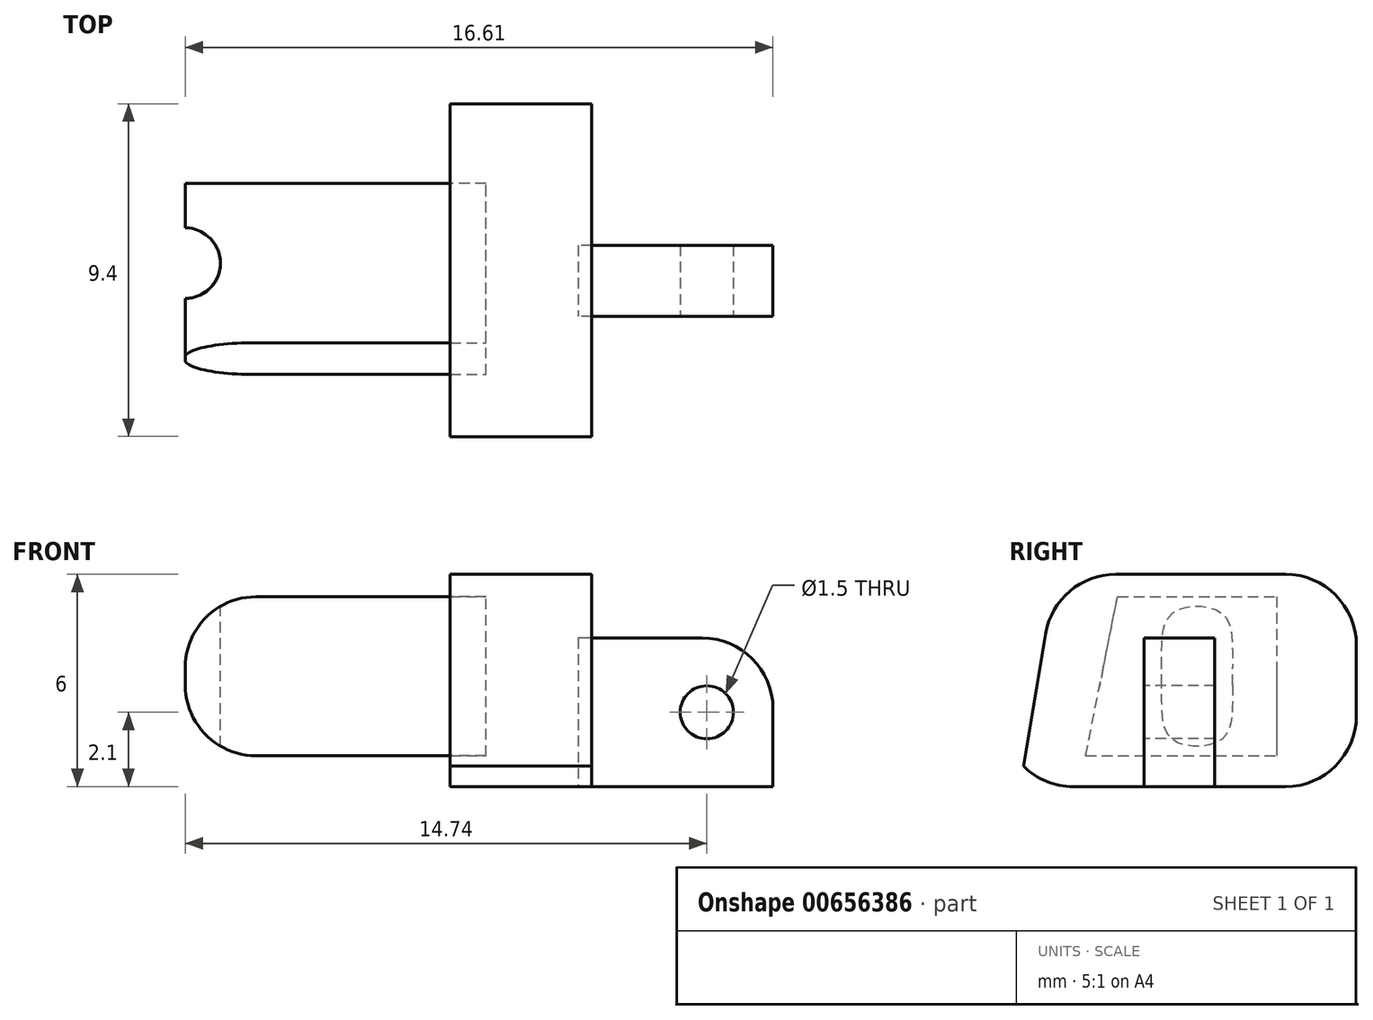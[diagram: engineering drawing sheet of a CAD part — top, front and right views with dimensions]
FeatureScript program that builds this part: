
annotation { "Feature Type Name" : "Feature", "Feature Type Description" : "" }
export const myFeature = defineFeature(function(context is Context, id is Id, definition is map)
    precondition{}
    {
        {
            var Q0;
            Q0=qCreatedBy(makeId("Top.planeOp"),FACE);
            var sketch = newSketch(context, id + "F0", { "sketchPlane" : qUnion([Q0])});
            skLineSegment(sketch, "E0.bottom", {"start": v(2, -5) * mm, "end": v(-2, -5) * mm});
            skLineSegment(sketch, "E0.top", {"start": v(2, 5) * mm, "end": v(-2, 5) * mm});
            skLineSegment(sketch, "E0.left", {"start": v(2, -5) * mm, "end": v(2, 5) * mm});
            skLineSegment(sketch, "E0.right", {"start": v(-2, -5) * mm, "end": v(-2, 5) * mm});
            skPoint(sketch, "E0.middle", {"position": v(0, 0) * mm});
            skLineSegment(sketch, "E1.bottom", {"start": v(8.83, 1) * mm, "end": v(3.33, 1) * mm});
            skLineSegment(sketch, "E1.top", {"start": v(8.83, -1) * mm, "end": v(3.33, -1) * mm});
            skLineSegment(sketch, "E1.left", {"start": v(8.83, 1) * mm, "end": v(8.83, -1) * mm});
            skLineSegment(sketch, "E1.right", {"start": v(3.33, 1) * mm, "end": v(3.33, -1) * mm});
            skPoint(sketch, "E1.middle", {"position": v(6.08, 0) * mm});
            skPoint(sketch, "E2.middle", {"position": v(-8.35, 0) * mm});
            skLineSegment(sketch, "E3.bottom", {"start": v(-3.78, -2.75) * mm, "end": v(-12.28, -2.75) * mm});
            skLineSegment(sketch, "E3.top", {"start": v(-3.78, 2.75) * mm, "end": v(-12.28, 2.75) * mm});
            skLineSegment(sketch, "E3.left", {"start": v(-3.78, -2.75) * mm, "end": v(-3.78, 2.75) * mm});
            skLineSegment(sketch, "E3.right", {"start": v(-12.28, -2.75) * mm, "end": v(-12.28, 2.75) * mm});
            skPoint(sketch, "E3.middle", {"position": v(-8.03, 0) * mm});
            skLineSegment(sketch, "E4", {"start": v(0, 0) * mm, "end": v(-1.4, 0) * mm, "construction": true});
            skLineSegment(sketch, "E5", {"start": v(-20.62, 0) * mm, "end": v(21.03, 0) * mm, "construction": true});
            skSolve(sketch);
        }
        {
            var Q0;
            Q0=makeQuery(id+"F0.imprint","IMPRINT",FACE,{"disambiguationData":[TD([[makeQuery(id+"F0.imprint","IMPRINT",EDGE,{"derivedFrom":sQuery(id+"F0.wireOp",EDGE,"E0.bottom")}),-1.0]])]});
            extrude(context, id + "F1", {"entities" : qUnion([Q0]), "depth" : 6 * mm, "offsetDistance" : 25 * mm});
        }
        {
            var Q0;
            Q0=makeQuery(id+"F0.imprint","IMPRINT",FACE,{"disambiguationData":[TD([[makeQuery(id+"F0.imprint","IMPRINT",EDGE,{"derivedFrom":sQuery(id+"F0.wireOp",EDGE,"E1.bottom")}),1.0]])]});
            extrude(context, id + "F2", {"entities" : qUnion([Q0]), "depth" : 4.2 * mm, "offsetDistance" : 25 * mm});
        }
        {
            var Q0;
            Q0=makeQuery(id+"F0.imprint","IMPRINT",FACE,{"disambiguationData":[TD([[makeQuery(id+"F0.imprint","IMPRINT",EDGE,{"derivedFrom":sQuery(id+"F0.wireOp",EDGE,"E3.bottom")}),-1.0]])]});
            extrude(context, id + "F3", {"entities" : qUnion([Q0]), "depth" : 4.5 * mm, "offsetDistance" : 25 * mm});
        }
        {
            var Q0;
            Q0=makeQuery(id+"F2.opExtrude","SWEPT_BODY",BODY,{"disambiguationData":[OSD([sQuery(id+"F0.wireOp",EDGE,"E1.bottom"),sQuery(id+"F0.wireOp",EDGE,"E1.top"),sQuery(id+"F0.wireOp",EDGE,"E1.left"),sQuery(id+"F0.wireOp",EDGE,"E1.right")])]});
            transform(context, id + "F4", {"entities" : qUnion([Q0]), "transformType" : TransformType.TRANSLATION_3D, "dx" : -1.71 * mm, "dy" : 0 * mm, "dz" : 0 * mm, "makeCopy" : false});
        }
        {
            var Q0;
            Q0=makeQuery(id+"F3.opExtrude","SWEPT_BODY",BODY,{"disambiguationData":[OSD([sQuery(id+"F0.wireOp",EDGE,"E3.bottom"),sQuery(id+"F0.wireOp",EDGE,"E3.top"),sQuery(id+"F0.wireOp",EDGE,"E3.left"),sQuery(id+"F0.wireOp",EDGE,"E3.right")])]});
            transform(context, id + "F5", {"entities" : qUnion([Q0]), "transformType" : TransformType.TRANSLATION_3D, "dx" : 2.8 * mm, "dy" : 0 * mm, "dz" : 0.87 * mm, "makeCopy" : false});
        }
        {
            var Q0;
            Q0=makeQuery(id+"F1.opExtrude","CAP_EDGE",EDGE,{"disambiguationData":[OSD([sQuery(id+"F0.wireOp",EDGE,"E0.bottom")])],"isStart":true});
            fillet(context, id + "F6", {"entities" : qUnion([Q0]), "radius" : 2 * mm, "tangentPropagation" : true, "allowEdgeOverflow" : false});
        }
        {
            var Q0;
            Q0=makeQuery(id+"F1.opExtrude","CAP_EDGE",EDGE,{"disambiguationData":[OSD([sQuery(id+"F0.wireOp",EDGE,"E0.bottom")])],"isStart":false});
            chamfer(context, id + "F7", {"entities" : qUnion([Q0]), "chamferType" : ChamferType.TWO_OFFSETS, "width1" : 9 * mm, "oppositeDirection" : false, "width2" : 1.5 * mm, "tangentPropagation" : true});
        }
        {
            var Q0;
            Q0=makeQuery(id+"F2.opExtrude","SWEPT_FACE",FACE,{"disambiguationData":[OSD([sQuery(id+"F0.wireOp",EDGE,"E1.top")])]});
            var sketch = newSketch(context, id + "F8", { "sketchPlane" : qUnion([Q0])});
            skCircle(sketch, "E6", {"center": v(5.25, 2.1) * mm, "radius": 0.75 * mm});
            skSolve(sketch);
        }
        {
            var Q0;
            Q0=makeQuery(id+"F8.imprint","IMPRINT",FACE,{"disambiguationData":[TD([[makeQuery(id+"F8.imprint","IMPRINT",EDGE,{"derivedFrom":sQuery(id+"F8.wireOp",EDGE,"E6")}),1.0]])]});
            extrude(context, id + "F9", {"entities" : qUnion([Q0]), "operationType" : NewBodyOperationType.REMOVE, "oppositeDirection" : true, "depth" : 5 * mm, "offsetDistance" : 25 * mm});
        }
        {
            var Q0;
            Q0=makeQuery(id+"F1.opExtrude","CAP_EDGE",EDGE,{"disambiguationData":[OSD([sQuery(id+"F0.wireOp",EDGE,"E0.top")])],"isStart":false});
            fillet(context, id + "F10", {"entities" : qUnion([Q0]), "radius" : 2 * mm, "tangentPropagation" : true, "allowEdgeOverflow" : false});
        }
        {
            var Q0;
            Q0=makeQuery(id+"F1.opExtrude","CAP_EDGE",EDGE,{"disambiguationData":[OSD([sQuery(id+"F0.wireOp",EDGE,"E0.top")])],"isStart":true});
            fillet(context, id + "F11", {"entities" : qUnion([Q0]), "radius" : 2 * mm, "tangentPropagation" : true, "allowEdgeOverflow" : false});
        }
        {
            var Q0;
            {var subQ0=sQuery(id+"F0.wireOp",EDGE,"E0.bottom");Q0=makeQuery(id+"F7.opChamfer","BLEND_EDGE",EDGE,{"blendedFrom":[makeQuery(id+"F1.opExtrude","CAP_EDGE",EDGE,{"disambiguationData":[OSD([subQ0])],"isStart":false}),makeQuery(id+"F1.opExtrude","CAP_FACE",FACE,{"disambiguationData":[OSD([subQ0,sQuery(id+"F0.wireOp",EDGE,"E0.top"),sQuery(id+"F0.wireOp",EDGE,"E0.left"),sQuery(id+"F0.wireOp",EDGE,"E0.right"),sQuery(id+"F0.wireOp",EDGE,"E3.bottom"),sQuery(id+"F0.wireOp",EDGE,"E3.top"),sQuery(id+"F0.wireOp",EDGE,"E3.left")])],"isStart":false})],"blendedInto":[makeQuery(id+"F1.opExtrude","CAP_FACE",FACE,{"disambiguationData":[OSD([subQ0,sQuery(id+"F0.wireOp",EDGE,"E0.top"),sQuery(id+"F0.wireOp",EDGE,"E0.left"),sQuery(id+"F0.wireOp",EDGE,"E0.right"),sQuery(id+"F0.wireOp",EDGE,"E3.bottom"),sQuery(id+"F0.wireOp",EDGE,"E3.top"),sQuery(id+"F0.wireOp",EDGE,"E3.left")])],"isStart":false})]});}
            fillet(context, id + "F12", {"entities" : qUnion([Q0]), "radius" : 2 * mm, "tangentPropagation" : true, "allowEdgeOverflow" : false});
        }
        {
            var Q0;
            Q0=makeQuery(id+"F3.opExtrude","CAP_EDGE",EDGE,{"disambiguationData":[OSD([sQuery(id+"F0.wireOp",EDGE,"E3.bottom")])],"isStart":false});
            chamfer(context, id + "F13", {"entities" : qUnion([Q0]), "chamferType" : ChamferType.TWO_OFFSETS, "width1" : 5 * mm, "oppositeDirection" : false, "width2" : 1 * mm, "tangentPropagation" : true});
        }
        {
            var Q0;
            Q0=makeQuery(id+"F3.opExtrude","CAP_FACE",FACE,{"disambiguationData":[OSD([sQuery(id+"F0.wireOp",EDGE,"E3.bottom"),sQuery(id+"F0.wireOp",EDGE,"E3.top"),sQuery(id+"F0.wireOp",EDGE,"E3.left"),sQuery(id+"F0.wireOp",EDGE,"E3.right")])],"isStart":false});
            var sketch = newSketch(context, id + "F14", { "sketchPlane" : qUnion([Q0])});
            skCircle(sketch, "E7", {"center": v(-9.5, 0.5) * mm, "radius": 1 * mm});
            skSolve(sketch);
        }
        {
            var Q0;
            Q0=makeQuery(id+"F2.opExtrude","CAP_EDGE",EDGE,{"disambiguationData":[OSD([sQuery(id+"F0.wireOp",EDGE,"E1.left")])],"isStart":false});
            fillet(context, id + "F15", {"entities" : qUnion([Q0]), "radius" : 2 * mm, "tangentPropagation" : true, "allowEdgeOverflow" : false});
        }
        {
            var Q0;
            {var subQ0=sQuery(id+"F14.wireOp",EDGE,"E7");var subQ1=makeQuery(id+"F3.opExtrude","CAP_EDGE",EDGE,{"disambiguationData":[OSD([sQuery(id+"F0.wireOp",EDGE,"E3.right")])],"isStart":false});var subQ2=makeQuery(id+"F14.imprint","INTERSECT",VERTEX,{"disambiguationData":[OD(0.0)],"derivedFrom":[subQ1,subQ0]});Q0=makeQuery(id+"F14.imprint","IMPRINT",FACE,{"disambiguationData":[TD([[makeQuery(id+"F14.imprint","IMPRINT",EDGE,{"disambiguationData":[TD([[subQ2,-1.0]])],"derivedFrom":subQ0}),1.0]])]});}
            var Q1;
            {var subQ0=sQuery(id+"F14.wireOp",EDGE,"E7");var subQ1=makeQuery(id+"F3.opExtrude","CAP_EDGE",EDGE,{"disambiguationData":[OSD([sQuery(id+"F0.wireOp",EDGE,"E3.right")])],"isStart":false});var subQ2=makeQuery(id+"F14.imprint","INTERSECT",VERTEX,{"disambiguationData":[OD(0.0)],"derivedFrom":[subQ1,subQ0]});Q1=makeQuery(id+"F14.imprint","IMPRINT",FACE,{"disambiguationData":[TD([[makeQuery(id+"F14.imprint","IMPRINT",EDGE,{"disambiguationData":[TD([[subQ2,1.0]])],"derivedFrom":subQ0}),1.0]])]});}
            extrude(context, id + "F16", {"entities" : qUnion([Q0, Q1]), "operationType" : NewBodyOperationType.REMOVE, "oppositeDirection" : true, "depth" : 4.78 * mm, "offsetDistance" : 25 * mm});
        }
        {
            var Q0;
            {var subQ0=sQuery(id+"F0.wireOp",EDGE,"E3.right");var subQ1=sQuery(id+"F0.wireOp",EDGE,"E3.top");Q0=makeQuery(id+"F16.boolean.opBoolean","SPLIT",EDGE,{"disambiguationData":[TD([makeQuery(id+"F3.opExtrude","SWEPT_FACE",FACE,{"disambiguationData":[OSD([subQ1])]})])],"derivedFrom":makeQuery(id+"F3.opExtrude","CAP_EDGE",EDGE,{"disambiguationData":[OSD([subQ0])],"isStart":false})});}
            var Q1;
            {var subQ0=sQuery(id+"F0.wireOp",EDGE,"E3.right");var subQ1=sQuery(id+"F0.wireOp",EDGE,"E3.bottom");Q1=makeQuery(id+"F16.boolean.opBoolean","SPLIT",EDGE,{"disambiguationData":[TD([makeQuery(id+"F13.opChamfer","BLEND_FACE",FACE,{"disambiguationData":[OSD([subQ1])]})])],"derivedFrom":makeQuery(id+"F3.opExtrude","CAP_EDGE",EDGE,{"disambiguationData":[OSD([subQ0])],"isStart":true})});}
            fillet(context, id + "F17", {"entities" : qUnion([Q0, Q1]), "radius" : 2 * mm, "tangentPropagation" : true, "allowEdgeOverflow" : false});
        }
    });
